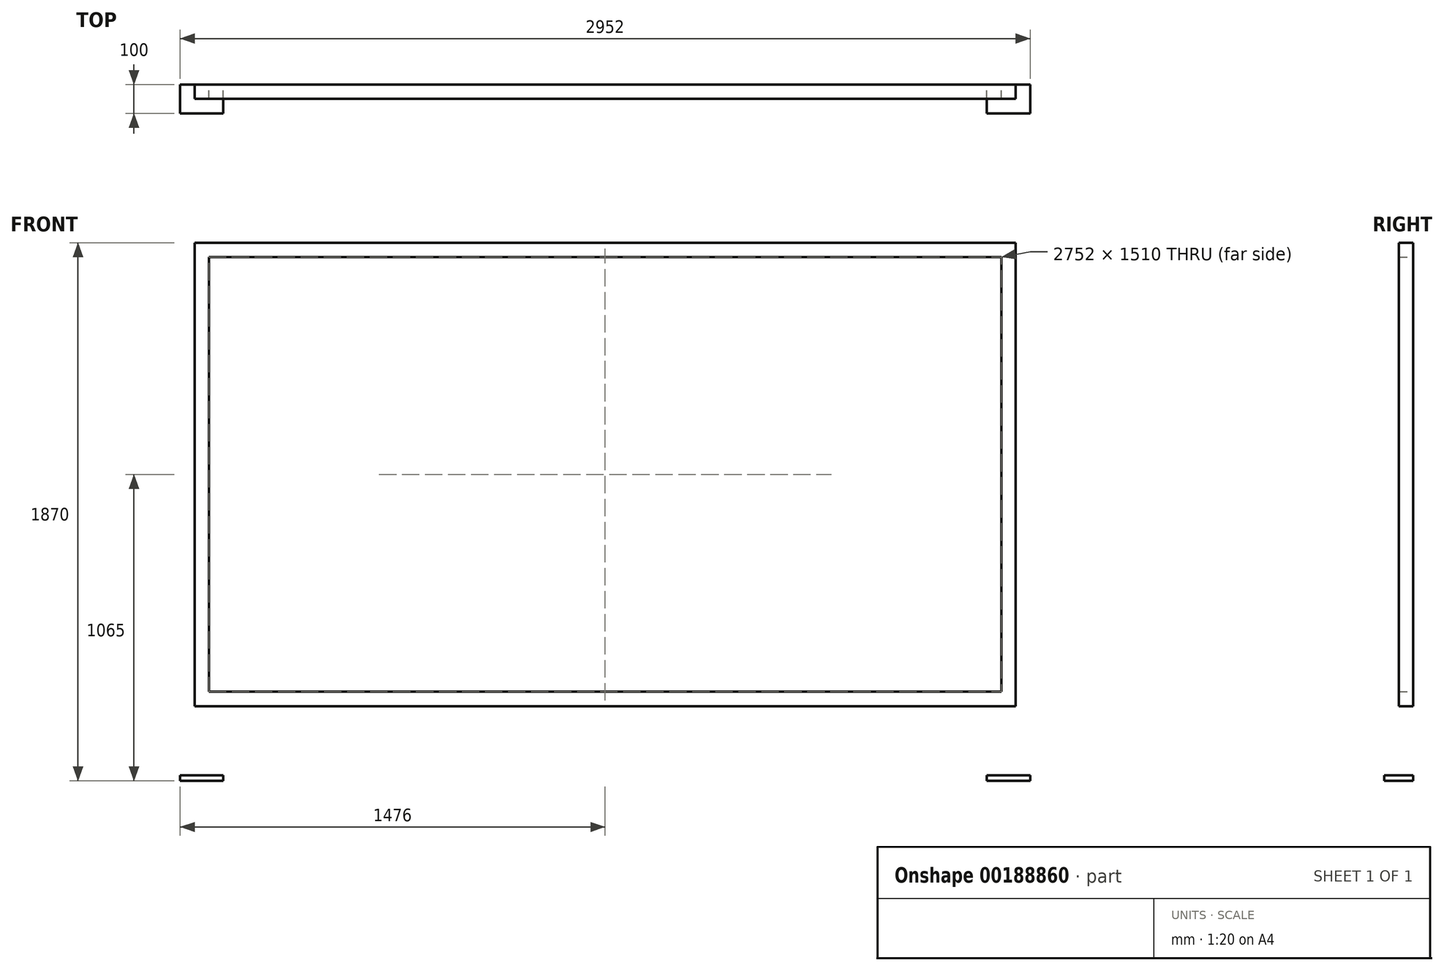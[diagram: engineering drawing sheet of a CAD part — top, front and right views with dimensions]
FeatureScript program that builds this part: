
annotation { "Feature Type Name" : "Feature", "Feature Type Description" : "" }
export const myFeature = defineFeature(function(context is Context, id is Id, definition is map)
    precondition{}
    {
        {
            var Q0;
            Q0=qCreatedBy(makeId("Front.planeOp"),FACE);
            var sketch = newSketch(context, id + "F0", { "sketchPlane" : qUnion([Q0])});
            skLineSegment(sketch, "E0.bottom", {"start": v(0, 0) * mm, "end": v(2852, 0) * mm});
            skLineSegment(sketch, "E0.top", {"start": v(0, -1610) * mm, "end": v(2852, -1610) * mm});
            skLineSegment(sketch, "E0.left", {"start": v(0, 0) * mm, "end": v(0, -1610) * mm});
            skLineSegment(sketch, "E0.right", {"start": v(2852, 0) * mm, "end": v(2852, -1610) * mm});
            skLineSegment(sketch, "E1.bottom", {"start": v(50, -50) * mm, "end": v(2802, -50) * mm});
            skLineSegment(sketch, "E1.top", {"start": v(50, -1560) * mm, "end": v(2802, -1560) * mm});
            skLineSegment(sketch, "E1.left", {"start": v(50, -50) * mm, "end": v(50, -1560) * mm});
            skLineSegment(sketch, "E1.right", {"start": v(2802, -50) * mm, "end": v(2802, -1560) * mm});
            skLineSegment(sketch, "E2.bottom", {"start": v(0, -1610) * mm, "end": v(50, -1610) * mm});
            skLineSegment(sketch, "E2.top", {"start": v(0, -1850) * mm, "end": v(50, -1850) * mm});
            skLineSegment(sketch, "E2.left", {"start": v(0, -1610) * mm, "end": v(0, -1850) * mm});
            skLineSegment(sketch, "E2.right", {"start": v(50, -1610) * mm, "end": v(50, -1850) * mm});
            skLineSegment(sketch, "E3.bottom", {"start": v(2852, -1610) * mm, "end": v(2802, -1610) * mm});
            skLineSegment(sketch, "E3.top", {"start": v(2852, -1850) * mm, "end": v(2802, -1850) * mm});
            skLineSegment(sketch, "E3.left", {"start": v(2852, -1610) * mm, "end": v(2852, -1850) * mm});
            skLineSegment(sketch, "E3.right", {"start": v(2802, -1610) * mm, "end": v(2802, -1850) * mm});
            skPoint(sketch, "E4.firstSnap0", {"position": v(25, -1850) * mm});
            skLineSegment(sketch, "E4.bottom", {"start": v(-50, -1850) * mm, "end": v(100, -1850) * mm});
            skLineSegment(sketch, "E4.top", {"start": v(-50, -1870) * mm, "end": v(100, -1870) * mm});
            skLineSegment(sketch, "E4.left", {"start": v(-50, -1850) * mm, "end": v(-50, -1870) * mm});
            skLineSegment(sketch, "E4.right", {"start": v(100, -1850) * mm, "end": v(100, -1870) * mm});
            skLineSegment(sketch, "E5.bottom", {"start": v(2752, -1850) * mm, "end": v(2902, -1850) * mm});
            skLineSegment(sketch, "E5.top", {"start": v(2752, -1870) * mm, "end": v(2902, -1870) * mm});
            skLineSegment(sketch, "E5.left", {"start": v(2752, -1850) * mm, "end": v(2752, -1870) * mm});
            skLineSegment(sketch, "E5.right", {"start": v(2902, -1850) * mm, "end": v(2902, -1870) * mm});
            skSolve(sketch);
        }
        {
            var Q0;
            Q0=makeQuery(id+"F0.imprint","IMPRINT",FACE,{"disambiguationData":[TD([[makeQuery(id+"F0.imprint","IMPRINT",EDGE,{"derivedFrom":sQuery(id+"F0.wireOp",EDGE,"E0.bottom")}),-1.0]])]});
            var Q1;
            Q1=makeQuery(id+"F0.imprint","IMPRINT",FACE,{"disambiguationData":[TD([[makeQuery(id+"F0.imprint","IMPRINT",EDGE,{"derivedFrom":sQuery(id+"F0.wireOp",EDGE,"E2.bottom")}),-1.0]])]});
            var Q2;
            Q2=makeQuery(id+"F0.imprint","IMPRINT",FACE,{"disambiguationData":[TD([[makeQuery(id+"F0.imprint","IMPRINT",EDGE,{"derivedFrom":sQuery(id+"F0.wireOp",EDGE,"E3.bottom")}),1.0]])]});
            extrude(context, id + "F1", {"entities" : qUnion([Q0, Q1, Q2]), "depth" : 50 * mm});
        }
        {
            var Q0;
            Q0=makeQuery(id+"F0.imprint","IMPRINT",FACE,{"disambiguationData":[TD([[makeQuery(id+"F0.imprint","IMPRINT",EDGE,{"derivedFrom":sQuery(id+"F0.wireOp",EDGE,"E4.top")}),1.0]])]});
            extrude(context, id + "F2", {"entities" : qUnion([Q0]), "operationType" : NewBodyOperationType.ADD, "depth" : 100 * mm});
        }
        {
            var Q0;
            Q0=makeQuery(id+"F0.imprint","IMPRINT",FACE,{"disambiguationData":[TD([[makeQuery(id+"F0.imprint","IMPRINT",EDGE,{"derivedFrom":sQuery(id+"F0.wireOp",EDGE,"E5.top")}),1.0]])]});
            extrude(context, id + "F3", {"entities" : qUnion([Q0]), "operationType" : NewBodyOperationType.ADD, "depth" : 100 * mm});
        }
    });
